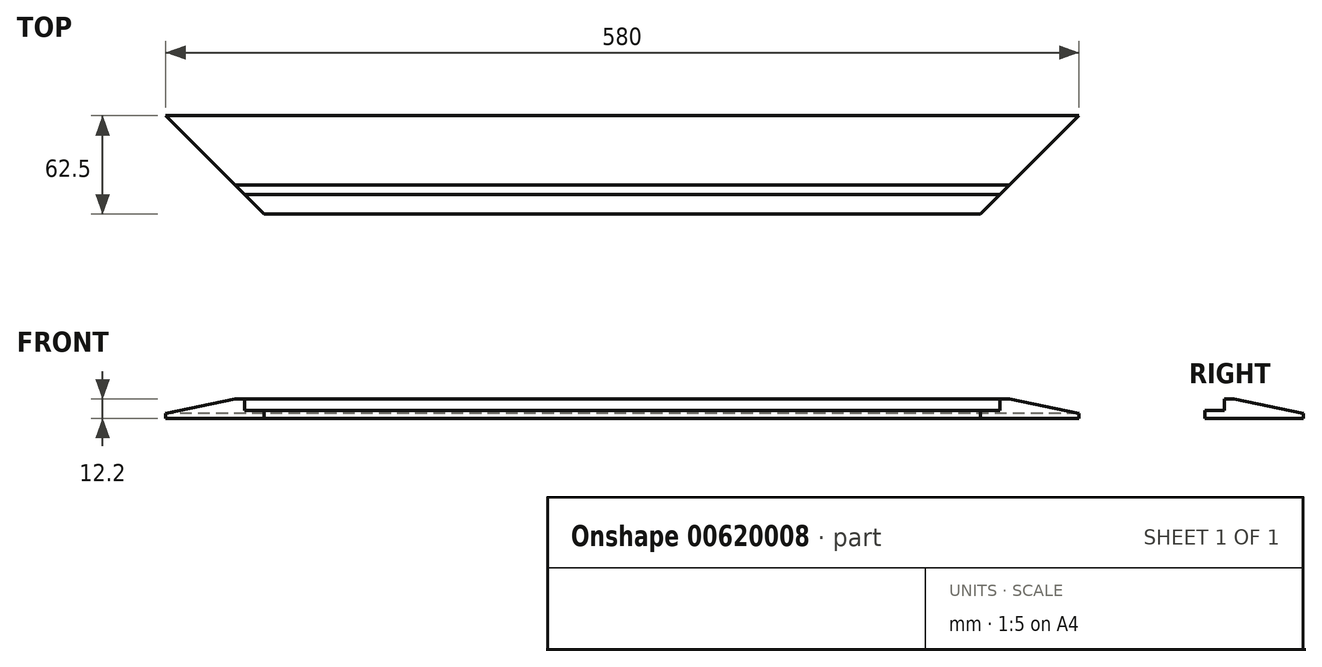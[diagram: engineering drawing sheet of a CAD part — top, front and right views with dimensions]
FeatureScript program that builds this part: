
annotation { "Feature Type Name" : "Feature", "Feature Type Description" : "" }
export const myFeature = defineFeature(function(context is Context, id is Id, definition is map)
    precondition{}
    {
        {
            var Q0;
            Q0=qCreatedBy(makeId("Right.planeOp"),FACE);
            var sketch = newSketch(context, id + "F0", { "sketchPlane" : qUnion([Q0])});
            skLineSegment(sketch, "E0", {"start": v(0, 0) * mm, "end": v(62.5, 0) * mm});
            skLineSegment(sketch, "E1", {"start": v(62.5, 0) * mm, "end": v(62.5, 3) * mm});
            skLineSegment(sketch, "E2", {"start": v(18.5, 12.2) * mm, "end": v(12.5, 12.2) * mm});
            skLineSegment(sketch, "E3", {"start": v(0, 5) * mm, "end": v(0, 0) * mm});
            skLineSegment(sketch, "E4.0", {"start": v(24.24, 11) * mm, "end": v(12.5, 11) * mm});
            skLineSegment(sketch, "E5.0", {"start": v(52.93, 5) * mm, "end": v(0, 5) * mm});
            skLineSegment(sketch, "E6.0", {"start": v(12.5, 12.2) * mm, "end": v(12.5, 0) * mm});
            skPoint(sketch, "E7.orphan", {"position": v(0, 12.2) * mm});
            skLineSegment(sketch, "E8.0", {"start": v(0, 3) * mm, "end": v(62.5, 3) * mm});
            skLineSegment(sketch, "E9.0", {"start": v(18.5, 12.2) * mm, "end": v(18.5, 0) * mm});
            skLineSegment(sketch, "E10", {"start": v(62.5, 3) * mm, "end": v(18.5, 12.2) * mm});
            skSolve(sketch);
        }
        {
            var Q0;
            Q0=qSketchRegion(id+"F0",true);
            extrude(context, id + "F1", {"entities" : qUnion([Q0]), "depth" : 580 * mm});
        }
        {
            var Q0;
            Q0=qCreatedBy(makeId("Top.planeOp"),FACE);
            var sketch = newSketch(context, id + "F2", { "sketchPlane" : qUnion([Q0])});
            skLineSegment(sketch, "E11", {"start": v(0, 0) * mm, "end": v(0, 62.5) * mm});
            skLineSegment(sketch, "E12", {"start": v(62.5, 0) * mm, "end": v(0, 62.5) * mm});
            skLineSegment(sketch, "E13", {"start": v(62.5, 0) * mm, "end": v(0, 0) * mm});
            skLineSegment(sketch, "E14", {"start": v(0, 0) * mm, "end": v(62.5, 0) * mm});
            skSolve(sketch);
        }
        {
            var Q0;
            Q0=qSketchRegion(id+"F2",true);
            extrude(context, id + "F3", {"entities" : qUnion([Q0]), "operationType" : NewBodyOperationType.REMOVE, "oppositeDirection" : true, "depth" : 100 * mm, "symmetric" : true});
        }
        {
            var Q0;
            Q0=qCreatedBy(makeId("Top.planeOp"),FACE);
            var sketch = newSketch(context, id + "F4", { "sketchPlane" : qUnion([Q0])});
            skLineSegment(sketch, "E15", {"start": v(0, 0) * mm, "end": v(517.5, 0) * mm});
            skLineSegment(sketch, "E16", {"start": v(517.5, 0) * mm, "end": v(580, 62.5) * mm});
            skLineSegment(sketch, "E17", {"start": v(580, 62.5) * mm, "end": v(580, 0) * mm});
            skLineSegment(sketch, "E18", {"start": v(580, 0) * mm, "end": v(517.5, 0) * mm});
            skSolve(sketch);
        }
        {
            var Q0;
            Q0=qSketchRegion(id+"F4",true);
            var Q1;
            Q1=sQuery(id+"F4.wireOp",EDGE,"E18");
            var Q2;
            Q2=sQuery(id+"F4.wireOp",EDGE,"E16");
            var Q3;
            Q3=sQuery(id+"F4.wireOp",EDGE,"E17");
            extrude(context, id + "F5", {"entities" : qUnion([Q0]), "operationType" : NewBodyOperationType.REMOVE, "surfaceEntities" : qUnion([Q1, Q2, Q3]), "oppositeDirection" : true, "depth" : 100 * mm, "symmetric" : true});
        }
    });
